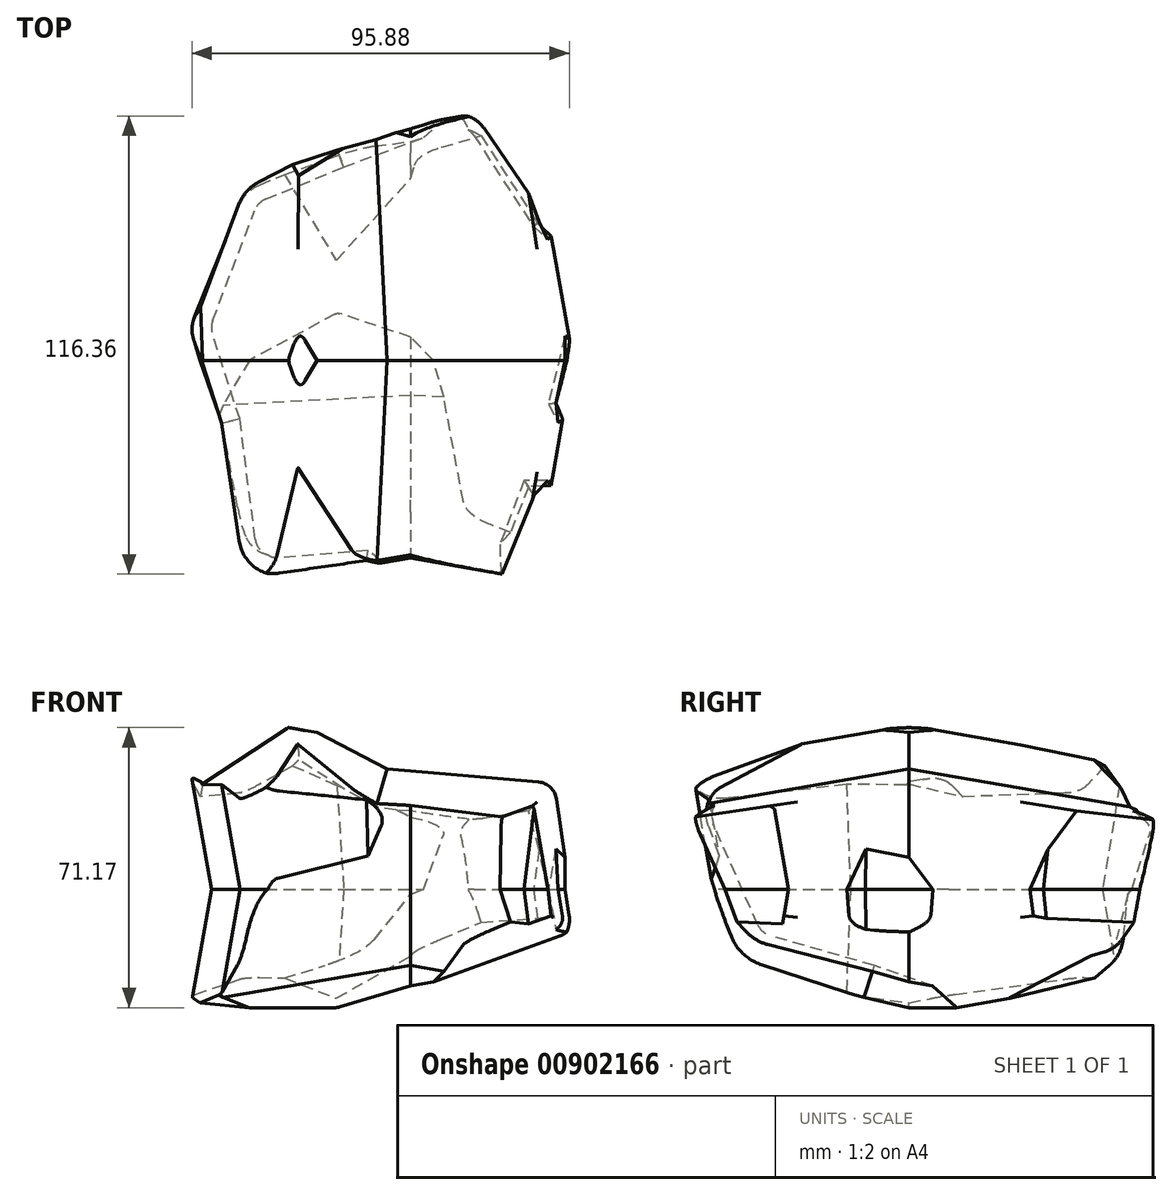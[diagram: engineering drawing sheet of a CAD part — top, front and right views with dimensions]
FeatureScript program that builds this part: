
annotation { "Feature Type Name" : "Feature", "Feature Type Description" : "" }
export const myFeature = defineFeature(function(context is Context, id is Id, definition is map)
    precondition{}
    {
        {
            var Q0;
            Q0=qCreatedBy(makeId("Front.planeOp"),FACE);
            var sketch = newSketch(context, id + "F0", { "sketchPlane" : qUnion([Q0])});
            skLineSegment(sketch, "E0", {"start": v(-61.27, 29.04) * mm, "end": v(-86.36, 7.16) * mm});
            skLineSegment(sketch, "E1", {"start": v(-87.68, 1.46) * mm, "end": v(-76.98, -24) * mm});
            skLineSegment(sketch, "E2", {"start": v(-72.84, -27.04) * mm, "end": v(-19.47, -32.16) * mm});
            skLineSegment(sketch, "E3", {"start": v(-17.29, -31.88) * mm, "end": v(37.96, -11.87) * mm});
            skLineSegment(sketch, "E4", {"start": v(41.2, -6.47) * mm, "end": v(37.03, 22.95) * mm});
            skLineSegment(sketch, "E5", {"start": v(32.51, 27.23) * mm, "end": v(-5.97, 30.55) * mm});
            skLineSegment(sketch, "E6", {"start": v(-5.97, 30.55) * mm, "end": v(-26.35, 41.13) * mm});
            skLineSegment(sketch, "E7", {"start": v(-31.4, 40.87) * mm, "end": v(-52.83, 26.75) * mm});
            skLineSegment(sketch, "E8", {"start": v(-52.83, 26.75) * mm, "end": v(-54.01, 28.3) * mm});
            skPoint(sketch, "E9.visualSharp", {"position": v(-57.25, 32.55) * mm});
            skArc(sketch, "E9.filletArc", {"start": v(-54.01, 28.3) * mm, "mid": v(-57.48, 30.24) * mm, "end": v(-61.27, 29.04) * mm});
            skPoint(sketch, "E10.visualSharp", {"position": v(-28.96, 42.48) * mm});
            skArc(sketch, "E10.filletArc", {"start": v(-26.35, 41.13) * mm, "mid": v(-28.92, 41.68) * mm, "end": v(-31.4, 40.87) * mm});
            skPoint(sketch, "E11.visualSharp", {"position": v(36.47, 26.89) * mm});
            skArc(sketch, "E11.filletArc", {"start": v(37.03, 22.95) * mm, "mid": v(35.52, 25.88) * mm, "end": v(32.51, 27.23) * mm});
            skPoint(sketch, "E12.visualSharp", {"position": v(41.78, -10.49) * mm});
            skArc(sketch, "E12.filletArc", {"start": v(37.96, -11.87) * mm, "mid": v(40.54, -9.74) * mm, "end": v(41.2, -6.47) * mm});
            skPoint(sketch, "E13.visualSharp", {"position": v(-18.35, -32.26) * mm});
            skArc(sketch, "E13.filletArc", {"start": v(-19.47, -32.16) * mm, "mid": v(-18.36, -32.14) * mm, "end": v(-17.29, -31.88) * mm});
            skPoint(sketch, "E14.visualSharp", {"position": v(-75.82, -26.75) * mm});
            skArc(sketch, "E14.filletArc", {"start": v(-76.98, -24) * mm, "mid": v(-75.33, -26.09) * mm, "end": v(-72.84, -27.04) * mm});
            skPoint(sketch, "E15.visualSharp", {"position": v(-89.08, 4.79) * mm});
            skArc(sketch, "E15.filletArc", {"start": v(-86.36, 7.16) * mm, "mid": v(-87.94, 4.52) * mm, "end": v(-87.68, 1.46) * mm});
            skSolve(sketch);
        }
        {
            var Q0;
            Q0 = qSketchRegion(id + "F0", true);
            extrude(context, id + "F1", {"entities" : qUnion([Q0]), "endBound" : BoundingType.SYMMETRIC, "depth" : 200 * mm, "offsetDistance" : 25 * mm, "hasDraft" : true, "draftAngle" : 10 * degree, "draftPullDirection" : true});
        }
        {
            var Q0;
            Q0=qCreatedBy(makeId("Right.planeOp"),FACE);
            var sketch = newSketch(context, id + "F2", { "sketchPlane" : qUnion([Q0])});
            skLineSegment(sketch, "E16", {"start": v(-49.74, 16.6) * mm, "end": v(-38.43, -8.98) * mm});
            skLineSegment(sketch, "E17", {"start": v(-35.25, -11.76) * mm, "end": v(-8.85, -19.4) * mm});
            skLineSegment(sketch, "E18", {"start": v(-8.85, -19.4) * mm, "end": v(13.63, -27.13) * mm});
            skLineSegment(sketch, "E19", {"start": v(16.9, -27.13) * mm, "end": v(49.65, -15.76) * mm});
            skLineSegment(sketch, "E20", {"start": v(52.85, -12.28) * mm, "end": v(59.6, 14.13) * mm});
            skLineSegment(sketch, "E21", {"start": v(57.6, 19.5) * mm, "end": v(35.38, 34.73) * mm});
            skLineSegment(sketch, "E22", {"start": v(32.55, 35.6) * mm, "end": v(-16.15, 35.6) * mm});
            skLineSegment(sketch, "E23", {"start": v(-18.06, 35.23) * mm, "end": v(-47.07, 23.24) * mm});
            skPoint(sketch, "E24.visualSharp", {"position": v(-51.8, 21.29) * mm});
            skArc(sketch, "E24.filletArc", {"start": v(-47.07, 23.24) * mm, "mid": v(-49.8, 20.49) * mm, "end": v(-49.74, 16.6) * mm});
            skPoint(sketch, "E25.visualSharp", {"position": v(-37.5, -11.12) * mm});
            skArc(sketch, "E25.filletArc", {"start": v(-38.43, -8.98) * mm, "mid": v(-37.15, -10.73) * mm, "end": v(-35.25, -11.76) * mm});
            skPoint(sketch, "E26.visualSharp", {"position": v(52.19, -14.88) * mm});
            skArc(sketch, "E26.filletArc", {"start": v(49.65, -15.76) * mm, "mid": v(51.69, -14.43) * mm, "end": v(52.85, -12.28) * mm});
            skPoint(sketch, "E27.visualSharp", {"position": v(60.48, 17.52) * mm});
            skArc(sketch, "E27.filletArc", {"start": v(59.6, 14.13) * mm, "mid": v(59.45, 17.13) * mm, "end": v(57.6, 19.5) * mm});
            skPoint(sketch, "E28.visualSharp", {"position": v(34.1, 35.6) * mm});
            skArc(sketch, "E28.filletArc", {"start": v(35.38, 34.73) * mm, "mid": v(34.03, 35.38) * mm, "end": v(32.55, 35.6) * mm});
            skPoint(sketch, "E29.visualSharp", {"position": v(-17.14, 35.6) * mm});
            skArc(sketch, "E29.filletArc", {"start": v(-16.15, 35.6) * mm, "mid": v(-17.13, 35.51) * mm, "end": v(-18.06, 35.23) * mm});
            skPoint(sketch, "E30.visualSharp", {"position": v(15.26, -27.7) * mm});
            skArc(sketch, "E30.filletArc", {"start": v(13.63, -27.13) * mm, "mid": v(15.26, -27.4) * mm, "end": v(16.9, -27.13) * mm});
            skSolve(sketch);
        }
        {
            var Q0;
            Q0 = qSketchRegion(id + "F2", true);
            extrude(context, id + "F3", {"entities" : qUnion([Q0]), "operationType" : NewBodyOperationType.INTERSECT, "endBound" : BoundingType.SYMMETRIC, "depth" : 200 * mm, "offsetDistance" : 25 * mm, "hasDraft" : true, "draftAngle" : 10 * degree});
        }
        {
            var Q0;
            Q0=qCreatedBy(makeId("Top.planeOp"),FACE);
            var sketch = newSketch(context, id + "F4", { "sketchPlane" : qUnion([Q0])});
            skLineSegment(sketch, "E31", {"start": v(-43.4, -14.88) * mm, "end": v(-39.51, -45.34) * mm});
            skLineSegment(sketch, "E32", {"start": v(-33.92, -49.67) * mm, "end": v(-10.69, -46.7) * mm});
            skLineSegment(sketch, "E33", {"start": v(-10.69, -46.7) * mm, "end": v(13.72, -56.05) * mm});
            skLineSegment(sketch, "E34", {"start": v(20.18, -53.17) * mm, "end": v(28.84, -30.56) * mm});
            skLineSegment(sketch, "E35", {"start": v(28.84, -30.56) * mm, "end": v(37.12, -30.56) * mm});
            skLineSegment(sketch, "E36", {"start": v(41.51, -23.17) * mm, "end": v(34.97, -11.12) * mm});
            skLineSegment(sketch, "E37", {"start": v(34.97, -11.12) * mm, "end": v(42.57, 19.96) * mm});
            skLineSegment(sketch, "E38", {"start": v(41.13, 24.8) * mm, "end": v(31.2, 34.1) * mm});
            skLineSegment(sketch, "E39", {"start": v(31.2, 34.1) * mm, "end": v(16.05, 57.16) * mm});
            skLineSegment(sketch, "E40", {"start": v(10.15, 59.11) * mm, "end": v(-17.03, 49.17) * mm});
            skLineSegment(sketch, "E41", {"start": v(-17.03, 49.17) * mm, "end": v(-36.89, 40.95) * mm});
            skLineSegment(sketch, "E42", {"start": v(-39.65, 38.11) * mm, "end": v(-50.31, 10.12) * mm});
            skLineSegment(sketch, "E43", {"start": v(-50.4, 6.8) * mm, "end": v(-43.4, -14.88) * mm});
            skPoint(sketch, "E44.visualSharp", {"position": v(45.52, -30.56) * mm});
            skArc(sketch, "E44.filletArc", {"start": v(37.12, -30.56) * mm, "mid": v(41.42, -28.11) * mm, "end": v(41.51, -23.17) * mm});
            skPoint(sketch, "E45.visualSharp", {"position": v(18.4, -57.84) * mm});
            skArc(sketch, "E45.filletArc", {"start": v(13.72, -56.05) * mm, "mid": v(17.55, -55.95) * mm, "end": v(20.18, -53.17) * mm});
            skPoint(sketch, "E46.visualSharp", {"position": v(43.26, 22.8) * mm});
            skArc(sketch, "E46.filletArc", {"start": v(42.57, 19.96) * mm, "mid": v(42.5, 22.57) * mm, "end": v(41.13, 24.8) * mm});
            skPoint(sketch, "E47.visualSharp", {"position": v(13.87, 60.48) * mm});
            skArc(sketch, "E47.filletArc", {"start": v(16.05, 57.16) * mm, "mid": v(13.44, 59.17) * mm, "end": v(10.15, 59.11) * mm});
            skPoint(sketch, "E48.visualSharp", {"position": v(-38.88, 40.13) * mm});
            skArc(sketch, "E48.filletArc", {"start": v(-36.89, 40.95) * mm, "mid": v(-38.56, 39.82) * mm, "end": v(-39.65, 38.11) * mm});
            skPoint(sketch, "E49.visualSharp", {"position": v(-50.94, 8.48) * mm});
            skArc(sketch, "E49.filletArc", {"start": v(-50.31, 10.12) * mm, "mid": v(-50.64, 8.47) * mm, "end": v(-50.4, 6.8) * mm});
            skPoint(sketch, "E50.visualSharp", {"position": v(-38.88, -50.3) * mm});
            skArc(sketch, "E50.filletArc", {"start": v(-39.51, -45.34) * mm, "mid": v(-37.61, -48.66) * mm, "end": v(-33.92, -49.67) * mm});
            skSolve(sketch);
        }
        {
            var Q0;
            Q0 = qSketchRegion(id + "F4", true);
            extrude(context, id + "F5", {"entities" : qUnion([Q0]), "operationType" : NewBodyOperationType.INTERSECT, "endBound" : BoundingType.SYMMETRIC, "depth" : 200 * mm, "offsetDistance" : 25 * mm, "hasDraft" : true, "draftAngle" : 10 * degree});
        }
    });
